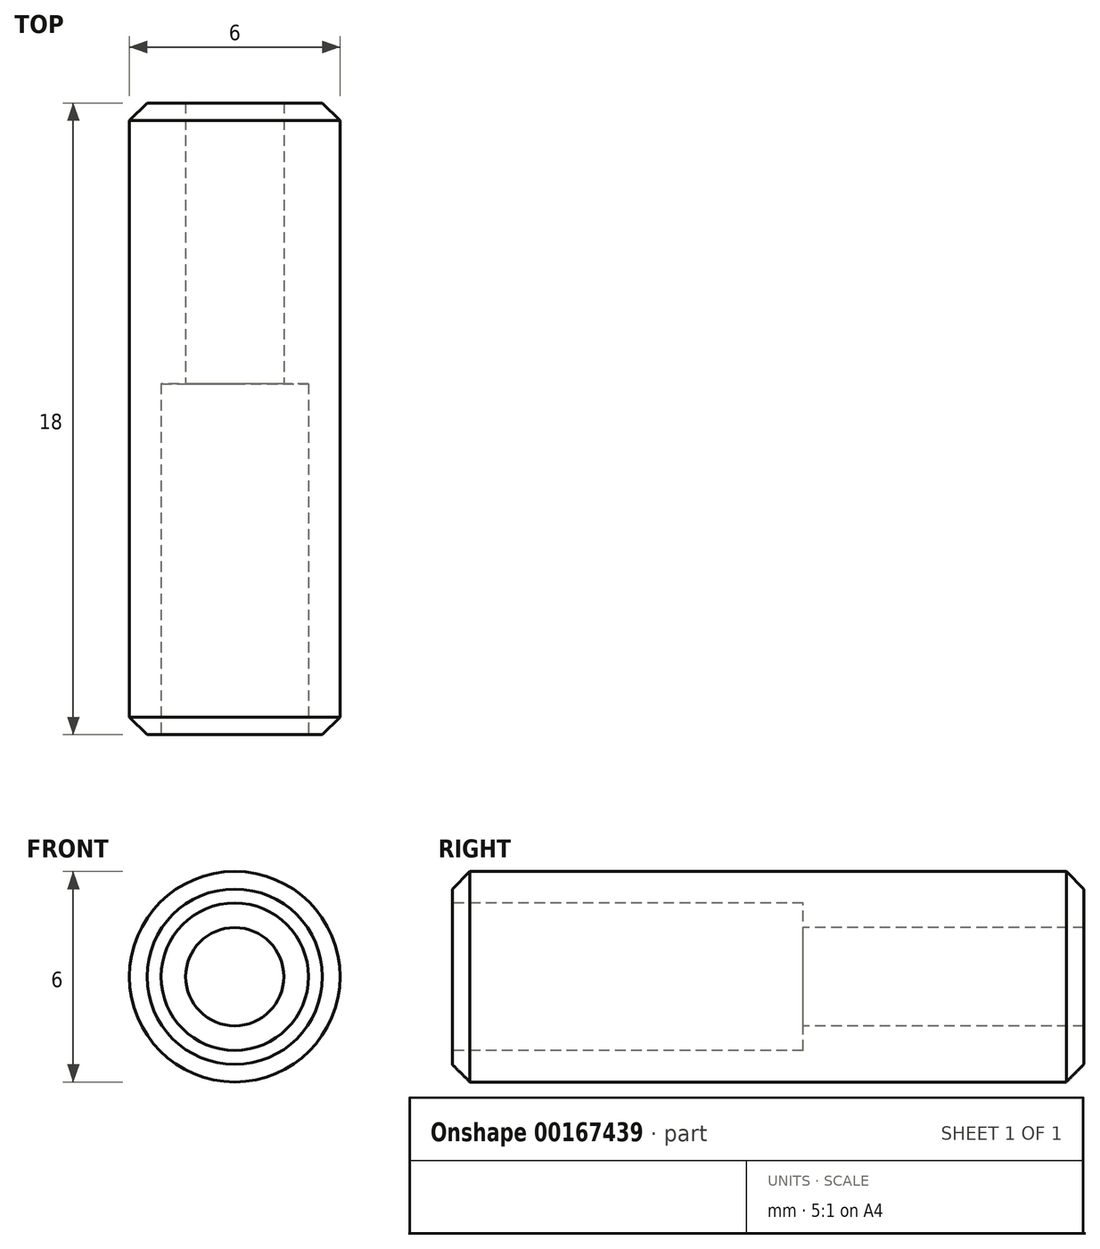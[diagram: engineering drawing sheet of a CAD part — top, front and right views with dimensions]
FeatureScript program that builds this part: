
annotation { "Feature Type Name" : "Feature", "Feature Type Description" : "" }
export const myFeature = defineFeature(function(context is Context, id is Id, definition is map)
    precondition{}
    {
        {
            var Q0;
            Q0=qCreatedBy(makeId("Front.planeOp"),FACE);
            var sketch = newSketch(context, id + "F0", { "sketchPlane" : qUnion([Q0])});
            skCircle(sketch, "E0", {"center": v(0, 0) * mm, "radius": 3 * mm});
            skSolve(sketch);
        }
        {
            var Q0;
            Q0=makeQuery(id+"F0.imprint","IMPRINT",FACE,{"disambiguationData":[TD([[makeQuery(id+"F0.imprint","IMPRINT",EDGE,{"derivedFrom":sQuery(id+"F0.wireOp",EDGE,"E0")}),1.0]])]});
            extrude(context, id + "F1", {"entities" : qUnion([Q0]), "oppositeDirection" : true, "depth" : 18 * mm});
        }
        {
            var Q0;
            Q0=makeQuery(id+"F1.opExtrude","CAP_FACE",FACE,{"disambiguationData":[OSD([sQuery(id+"F0.wireOp",EDGE,"E0")])],"isStart":true});
            var sketch = newSketch(context, id + "F2", { "sketchPlane" : qUnion([Q0])});
            skCircle(sketch, "E1", {"center": v(0, 0) * mm, "radius": 2.1 * mm});
            skSolve(sketch);
        }
        {
            var Q0;
            Q0=makeQuery(id+"F2.imprint","IMPRINT",FACE,{"disambiguationData":[TD([[makeQuery(id+"F2.imprint","IMPRINT",EDGE,{"derivedFrom":sQuery(id+"F2.wireOp",EDGE,"E1")}),1.0]])]});
            extrude(context, id + "F3", {"entities" : qUnion([Q0]), "operationType" : NewBodyOperationType.REMOVE, "oppositeDirection" : true, "depth" : 10 * mm});
        }
        {
            var Q0;
            Q0=qCreatedBy(makeId("Front.planeOp"),FACE);
            var sketch = newSketch(context, id + "F4", { "sketchPlane" : qUnion([Q0])});
            skCircle(sketch, "E2", {"center": v(0, 0) * mm, "radius": 1.4 * mm});
            skSolve(sketch);
        }
        {
            var Q0;
            Q0=makeQuery(id+"F4.imprint","IMPRINT",FACE,{"disambiguationData":[TD([[makeQuery(id+"F4.imprint","IMPRINT",EDGE,{"derivedFrom":sQuery(id+"F4.wireOp",EDGE,"E2")}),1.0]])]});
            extrude(context, id + "F5", {"entities" : qUnion([Q0]), "operationType" : NewBodyOperationType.REMOVE, "endBound" : BoundingType.THROUGH_ALL, "oppositeDirection" : true, "depth" : 25.4 * mm});
        }
        {
            var Q0;
            Q0=makeQuery(id+"F1.opExtrude","CAP_EDGE",EDGE,{"disambiguationData":[OSD([sQuery(id+"F0.wireOp",EDGE,"E0")])],"isStart":true});
            chamfer(context, id + "F6", {"entities" : qUnion([Q0]), "width" : .5 * mm, "tangentPropagation" : true});
        }
        {
            var Q0;
            Q0=makeQuery(id+"F1.opExtrude","CAP_EDGE",EDGE,{"disambiguationData":[OSD([sQuery(id+"F0.wireOp",EDGE,"E0")])],"isStart":false});
            chamfer(context, id + "F7", {"entities" : qUnion([Q0]), "width" : .5 * mm, "tangentPropagation" : true});
        }
    });
